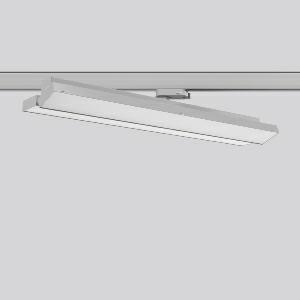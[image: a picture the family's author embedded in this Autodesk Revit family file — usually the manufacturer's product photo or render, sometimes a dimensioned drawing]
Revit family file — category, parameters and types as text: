
# Revit family: tx-move_742164_004_2_da2c
name_source: partatom
category: Lighting Fixtures
units: mm (PartAtom-declared; Revit-internal decimal feet)

## family parameters
Cut with Voids When Loaded = No
Host = Face
Light Source = No
Part Type = Normal
Room Calculation Point = No
Round Connector Dimension = Use Diameter
Shared = No

## types (1)
- MultiLumen 1 (1 x LED Modul 927, 1800 lm, 2700)
    Apparent Load = 38 VA
    CIE Flux Codes = 47 79 96 100 100
    Color Rendering = 92
    Color Temperature = 2700
    Default Elevation = 1800 mm  [stored 5.90551 ft]
    Description = Series: TX-MOVE
Multifunctional surface-mounted spotlight for area lighting. Very flat design. Housing: sheet steel, powder-coated. Rotation range: 356°. Swivel range: 90°. Consistent alignment possible with visible tilt scale. High-efficiency LED units with flush-mounted opal diffuser made of non-yellowing PMMA. Symmetrical wide beam light distribution. Best colour rendering with CRI >90 for fresh products and coloured textiles. With multi adaptor for 3-circuit tracks 230 V. Suitable for Track on ceiling. MultiLumen: Luminous flux adjustable in 3 steps. Factory setting is the highest luminous flux. Environmentally friendly and resource-saving due to replaceable and recyclable components. 
Colour: silver, matt (approx. RAL 9006)
Length: 570 mm
Width: 119 mm
Height: 92 mm
Lamp: LED
Socket: without socket
Colour temperature: 2700K
Colour rendering index (CRI): 90
System power: 38 W
Rated luminous flux: 3600 lm
Luminous efficiency: 95 lm/W
System power 2: 51 W
Rated luminous flux 2: 4700 lm
Luminous efficiency 2: 92 lm/W
System power 3: 62 W
Rated luminous flux 3: 5550 lm
Luminous efficiency 3: 90 lm/W
Control gear: Regulated power supply
Protection class: I
Type of protection: IP 20
    Height = 75 mm
    Lamp = 1 x LED Modul 927
    Lamp Light Flux = 1800 lm
    Lamp count = 1
    Length = 569 mm
    Lifetime = 50000 h
    Luminous efficacy = 95 lm/W
    Manufacturer = RZB
    ModVariant = No
    Model = 742164.004.2
    Mounting Place = Ceiling
    Mounting Type = Surface mounted
    Number of Poles = 1
    OnlyDefault = Yes
    Power Factor = 1
    Product Name = TX-MOVE
    Product group = Track mounted projectors
    ProductGroupID = 301
    Protection Class = Protection class I
    Protection Degree = IP 20
    RLX_Detail_Level = 1
    RLX_Emergency_Light_Flux = 0 lm
    RLX_Emergency_Type = 0
    RLX_Emergency_Type_DB = No
    RlxData = <blob elided: 32521 chars, md5=2843b272>
    Socket = socket
    Standby Power = 0 W
    System Light Flux = 3600 lm
    System Power = 38 W
    Type Comments = MultiLumen 1
    Type Image = 742164.004.jpg
    URL = http://relux.com
    VarID = multilumen_1
    Voltage = 0 V
    Weight = 0.00 kg
    Width = 119 mm

note: [stored X ft] marks values corroborated as IEEE doubles in the binary element streams (Revit-internal decimal feet)

## geometry (parser evidence)
native form markers: Blend x4, Sweep x17
no freeform markers — native parametric forms only
